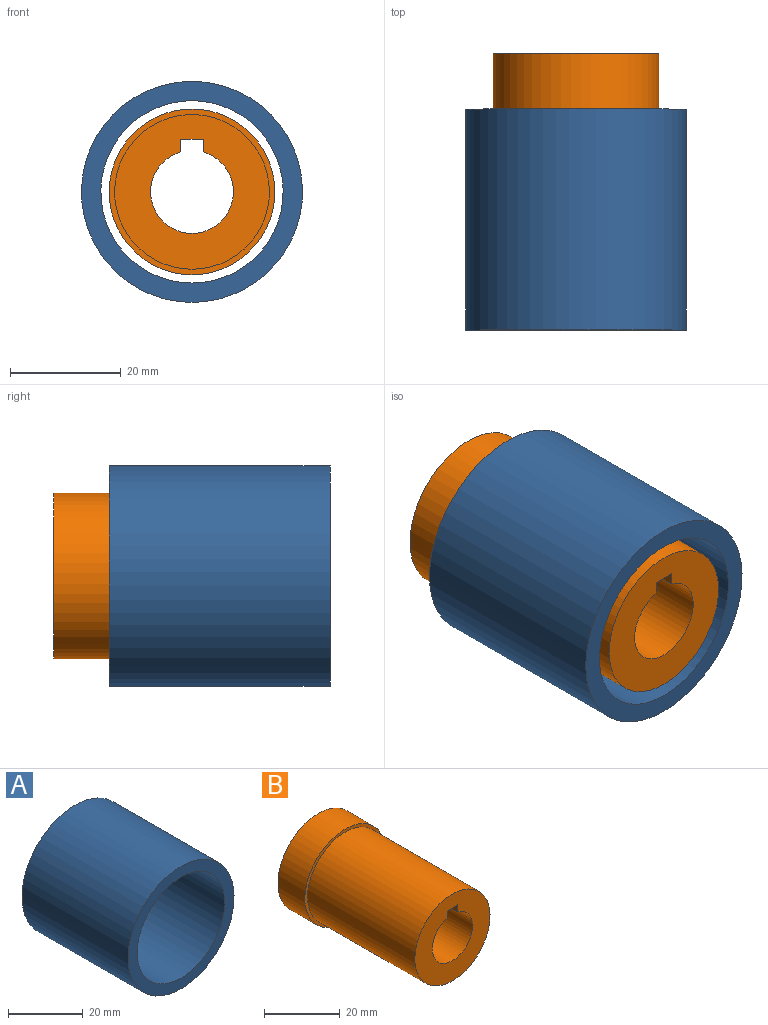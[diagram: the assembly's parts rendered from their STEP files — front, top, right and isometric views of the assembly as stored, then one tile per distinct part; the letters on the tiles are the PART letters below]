
ASSEMBLY  parts=2 mates=1
PART A: 4 faces, bbox 40x40x40 mm
  f0: cylinder r=16.5mm len=40mm, axis (0,1,0), area 4146.9mm2, adj f2,f3
  f1: cylinder r=20mm len=40mm, axis (0,1,0), area 5026.5mm2, adj f2,f3
  f2: plane 40x40mm, normal (0,-1,0), area 401.3mm2, adj f0,f1
  f3: plane 40x40mm, normal (0,1,0), area 401.3mm2, adj f0,f1
PART B: 9 faces, bbox 30x50x30 mm
  f0: plane 30x30mm, normal (0,1,0), area 521.8mm2, adj f2,f5,f6,f7,f8
  f1: plane 28x28mm, normal (0,-1,0), area 430.7mm2, adj f4,f5,f6,f7,f8
  f2: cylinder r=15mm len=30mm, axis (0,1,0), area 942.5mm2, adj f0,f3
  f3: plane 30x30mm, normal (0,-1,0), area 91.1mm2, adj f2,f4
  f4: cylinder r=14mm len=40mm, axis (0,1,0), area 3518.6mm2, adj f1,f3
  f5: plane 50x2.27mm, normal (-1,0,0), area 113.6mm2, adj f0,f1,f6,f8
  f6: plane 50x4mm, normal (0,0,-1), area 200mm2, adj f0,f1,f5,f7
  f7: plane 50x2.27mm, normal (1,0,0), area 113.6mm2, adj f0,f1,f6,f8
  f8: cylinder r=7.5mm len=50mm, axis (0,-1,0), area 2153.7mm2, adj f0,f1,f5,f7
PLACE A t=(-40.42,-6.44,-4.65)mm
PLACE B t=(-40.42,3.56,-4.65)mm
MATE fastened B.f4 <-> A.f0  axis (0,1,0) through (-40.42,-26.44,-4.65)mm
